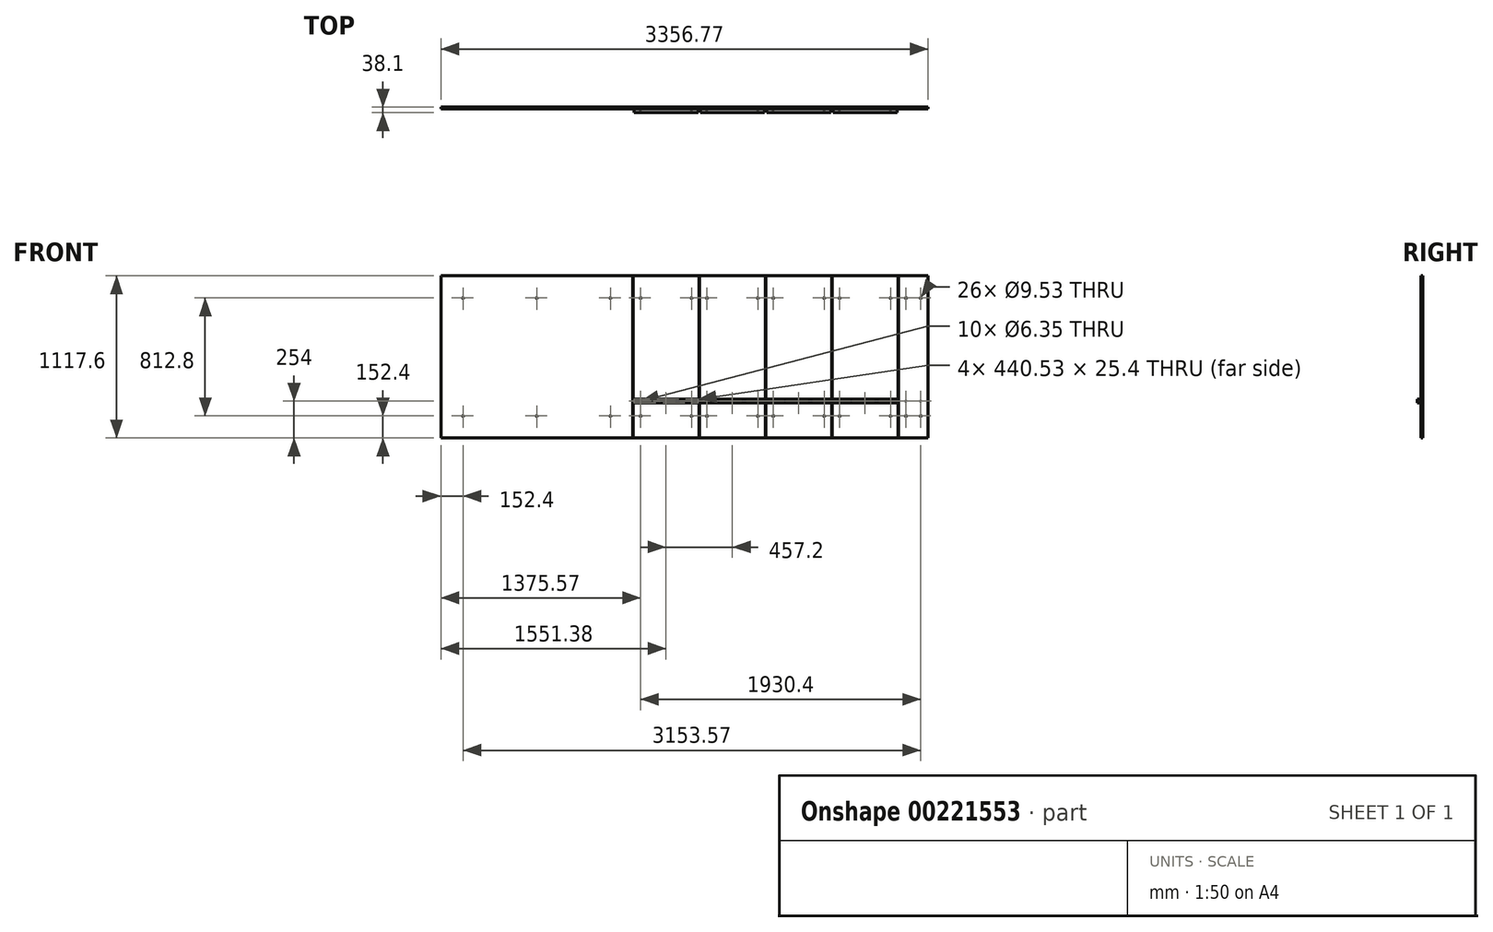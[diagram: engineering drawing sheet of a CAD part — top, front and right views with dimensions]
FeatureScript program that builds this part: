
annotation { "Feature Type Name" : "Feature", "Feature Type Description" : "" }
export const myFeature = defineFeature(function(context is Context, id is Id, definition is map)
    precondition{}
    {
        {
            var Q0;
            Q0=qCreatedBy(makeId("Front.planeOp"),FACE);
            var sketch = newSketch(context, id + "F0", { "sketchPlane" : qUnion([Q0])});
            skLineSegment(sketch, "E0.bottom", {"start": v(0, 0) * mm, "end": v(1320.8, 0) * mm});
            skLineSegment(sketch, "E0.top", {"start": v(0, 1117.6) * mm, "end": v(1320.8, 1117.6) * mm});
            skLineSegment(sketch, "E0.left", {"start": v(0, 0) * mm, "end": v(0, 1117.6) * mm});
            skLineSegment(sketch, "E0.right", {"start": v(1320.8, 0) * mm, "end": v(1320.8, 1117.6) * mm});
            skLineSegment(sketch, "E1.bottom", {"start": v(1320.8, 0) * mm, "end": v(1324.77, 0) * mm});
            skLineSegment(sketch, "E1.top", {"start": v(1320.8, 1117.6) * mm, "end": v(1324.77, 1117.6) * mm});
            skLineSegment(sketch, "E1.right", {"start": v(1324.77, 0) * mm, "end": v(1324.77, 1117.6) * mm});
            skLineSegment(sketch, "E2.bottom", {"start": v(1324.77, 0) * mm, "end": v(1778, 0) * mm});
            skLineSegment(sketch, "E2.top", {"start": v(1324.77, 1117.6) * mm, "end": v(1778, 1117.6) * mm});
            skLineSegment(sketch, "E2.right", {"start": v(1778, 0) * mm, "end": v(1778, 1117.6) * mm});
            skLineSegment(sketch, "E3.1.0.1", {"start": v(1781.97, 1117.6) * mm, "end": v(2235.2, 1117.6) * mm});
            skLineSegment(sketch, "E3.1.0.2", {"start": v(2235.2, 0) * mm, "end": v(2235.2, 1117.6) * mm});
            skLineSegment(sketch, "E3.1.0.3", {"start": v(1781.97, 0) * mm, "end": v(1781.97, 1117.6) * mm});
            skLineSegment(sketch, "E3.1.0.4", {"start": v(1781.97, 0) * mm, "end": v(1781.97, 1117.6) * mm});
            skLineSegment(sketch, "E3.1.0.6", {"start": v(1778, 1117.6) * mm, "end": v(1781.97, 1117.6) * mm});
            skLineSegment(sketch, "E3.1.0.7", {"start": v(1781.97, 0) * mm, "end": v(2235.2, 0) * mm});
            skLineSegment(sketch, "E3.1.0.8", {"start": v(1778, 0) * mm, "end": v(1781.97, 0) * mm});
            skLineSegment(sketch, "E3.2.0.0", {"start": v(2235.2, 0) * mm, "end": v(2235.2, 1117.6) * mm});
            skLineSegment(sketch, "E3.2.0.1", {"start": v(2239.17, 1117.6) * mm, "end": v(2692.4, 1117.6) * mm});
            skLineSegment(sketch, "E3.2.0.2", {"start": v(2692.4, 0) * mm, "end": v(2692.4, 1117.6) * mm});
            skLineSegment(sketch, "E3.2.0.3", {"start": v(2239.17, 0) * mm, "end": v(2239.17, 1117.6) * mm});
            skLineSegment(sketch, "E3.2.0.4", {"start": v(2239.17, 0) * mm, "end": v(2239.17, 1117.6) * mm});
            skLineSegment(sketch, "E3.2.0.5", {"start": v(2235.2, 0) * mm, "end": v(2235.2, 1117.6) * mm});
            skLineSegment(sketch, "E3.2.0.6", {"start": v(2235.2, 1117.6) * mm, "end": v(2239.17, 1117.6) * mm});
            skLineSegment(sketch, "E3.2.0.7", {"start": v(2239.17, 0) * mm, "end": v(2692.4, 0) * mm});
            skLineSegment(sketch, "E3.2.0.8", {"start": v(2235.2, 0) * mm, "end": v(2239.17, 0) * mm});
            skLineSegment(sketch, "E3.direction1", {"start": v(1320.8, 0) * mm, "end": v(1778, 0) * mm, "construction": true});
            skLineSegment(sketch, "E4.3.3.0", {"start": v(2696.37, 1117.6) * mm, "end": v(3149.6, 1117.6) * mm});
            skLineSegment(sketch, "E4.6.3.0", {"start": v(3149.6, 0) * mm, "end": v(3149.6, 1117.6) * mm});
            skLineSegment(sketch, "E4.9.3.0", {"start": v(2696.37, 0) * mm, "end": v(2696.37, 1117.6) * mm});
            skLineSegment(sketch, "E4.12.3.0", {"start": v(2696.37, 0) * mm, "end": v(2696.37, 1117.6) * mm});
            skLineSegment(sketch, "E4.18.3.0", {"start": v(2692.4, 1117.6) * mm, "end": v(2696.37, 1117.6) * mm});
            skLineSegment(sketch, "E4.21.3.0", {"start": v(2696.37, 0) * mm, "end": v(3149.6, 0) * mm});
            skLineSegment(sketch, "E4.24.3.0", {"start": v(2692.4, 0) * mm, "end": v(2696.37, 0) * mm});
            skLineSegment(sketch, "E5.9.4.0", {"start": v(3153.57, 0) * mm, "end": v(3153.57, 1117.6) * mm});
            skLineSegment(sketch, "E5.12.4.0", {"start": v(3153.57, 0) * mm, "end": v(3153.57, 1117.6) * mm});
            skLineSegment(sketch, "E5.18.4.0", {"start": v(3149.6, 1117.6) * mm, "end": v(3153.57, 1117.6) * mm});
            skLineSegment(sketch, "E5.24.4.0", {"start": v(3149.6, 0) * mm, "end": v(3153.57, 0) * mm});
            skLineSegment(sketch, "E6.bottom", {"start": v(3153.57, 0) * mm, "end": v(3356.77, 0) * mm});
            skLineSegment(sketch, "E6.top", {"start": v(3153.57, 1117.6) * mm, "end": v(3356.77, 1117.6) * mm});
            skLineSegment(sketch, "E6.right", {"start": v(3356.77, 0) * mm, "end": v(3356.77, 1117.6) * mm});
            skPoint(sketch, "E7.firstSnap0", {"position": v(0, 558.8) * mm});
            skLineSegment(sketch, "E7.bottom", {"start": v(-26.7, 558.8) * mm, "end": v(0, 558.8) * mm});
            skLineSegment(sketch, "E7.top", {"start": v(-26.7, 558.8) * mm, "end": v(0, 558.8) * mm});
            skLineSegment(sketch, "E7.left", {"start": v(-26.7, 558.8) * mm, "end": v(-26.7, 558.8) * mm});
            skLineSegment(sketch, "E7.right", {"start": v(0, 558.8) * mm, "end": v(0, 558.8) * mm});
            skLineSegment(sketch, "E8", {"start": v(0, 0) * mm, "end": v(0, 152.4) * mm});
            skLineSegment(sketch, "E9", {"start": v(0, 152.4) * mm, "end": v(152.4, 152.4) * mm});
            skLineSegment(sketch, "E10", {"start": v(152.4, 152.4) * mm, "end": v(660.4, 152.4) * mm});
            skLineSegment(sketch, "E11", {"start": v(660.4, 152.4) * mm, "end": v(1168.4, 152.4) * mm});
            skLineSegment(sketch, "E12", {"start": v(1168.4, 152.4) * mm, "end": v(1168.4, 965.2) * mm});
            skLineSegment(sketch, "E13", {"start": v(1168.4, 965.2) * mm, "end": v(660.4, 965.2) * mm});
            skLineSegment(sketch, "E14", {"start": v(660.4, 965.2) * mm, "end": v(152.4, 965.2) * mm});
            skCircle(sketch, "E15", {"center": v(152.4, 965.2) * mm, "radius": 4.76 * mm});
            skCircle(sketch, "E16", {"center": v(660.4, 965.2) * mm, "radius": 4.76 * mm});
            skCircle(sketch, "E17", {"center": v(1168.4, 965.2) * mm, "radius": 4.76 * mm});
            skCircle(sketch, "E18", {"center": v(152.4, 152.4) * mm, "radius": 4.76 * mm});
            skCircle(sketch, "E19", {"center": v(660.4, 152.4) * mm, "radius": 4.76 * mm});
            skCircle(sketch, "E20", {"center": v(1168.4, 152.4) * mm, "radius": 4.76 * mm});
            skLineSegment(sketch, "E21", {"start": v(1168.4, 152.4) * mm, "end": v(1320.8, 152.4) * mm});
            skLineSegment(sketch, "E22", {"start": v(1320.8, 152.4) * mm, "end": v(1324.77, 152.28) * mm});
            skLineSegment(sketch, "E23", {"start": v(1324.77, 152.28) * mm, "end": v(1375.57, 152.4) * mm});
            skPoint(sketch, "E24.endSnap0", {"position": v(1244.6, 152.4) * mm});
            skLineSegment(sketch, "E25", {"start": v(1778, 152.4) * mm, "end": v(1727.2, 152.4) * mm});
            skCircle(sketch, "E26", {"center": v(1375.57, 152.4) * mm, "radius": 4.76 * mm});
            skCircle(sketch, "E27", {"center": v(1727.2, 152.4) * mm, "radius": 4.76 * mm});
            skCircle(sketch, "E28.0.1.0", {"center": v(1375.57, 965.2) * mm, "radius": 4.76 * mm});
            skCircle(sketch, "E28.0.1.1", {"center": v(1727.2, 965.2) * mm, "radius": 4.76 * mm});
            skCircle(sketch, "E28.1.0.0", {"center": v(1832.77, 152.4) * mm, "radius": 4.76 * mm});
            skCircle(sketch, "E28.1.0.1", {"center": v(2184.4, 152.4) * mm, "radius": 4.76 * mm});
            skCircle(sketch, "E28.1.1.0", {"center": v(1832.77, 965.2) * mm, "radius": 4.76 * mm});
            skCircle(sketch, "E28.1.1.1", {"center": v(2184.4, 965.2) * mm, "radius": 4.76 * mm});
            skCircle(sketch, "E28.2.0.0", {"center": v(2289.97, 152.4) * mm, "radius": 4.76 * mm});
            skCircle(sketch, "E28.2.0.1", {"center": v(2641.6, 152.4) * mm, "radius": 4.76 * mm});
            skCircle(sketch, "E28.2.1.0", {"center": v(2289.97, 965.2) * mm, "radius": 4.76 * mm});
            skCircle(sketch, "E28.2.1.1", {"center": v(2641.6, 965.2) * mm, "radius": 4.76 * mm});
            skCircle(sketch, "E28.3.0.0", {"center": v(2747.17, 152.4) * mm, "radius": 4.76 * mm});
            skCircle(sketch, "E28.3.0.1", {"center": v(3098.8, 152.4) * mm, "radius": 4.76 * mm});
            skCircle(sketch, "E28.3.1.0", {"center": v(2747.17, 965.2) * mm, "radius": 4.76 * mm});
            skCircle(sketch, "E28.3.1.1", {"center": v(3098.8, 965.2) * mm, "radius": 4.76 * mm});
            skCircle(sketch, "E28.4.0.0", {"center": v(3204.37, 152.4) * mm, "radius": 4.76 * mm});
            skCircle(sketch, "E28.4.1.0", {"center": v(3204.37, 965.2) * mm, "radius": 4.76 * mm});
            skLineSegment(sketch, "E28.direction1", {"start": v(1375.57, 152.4) * mm, "end": v(1832.77, 152.4) * mm, "construction": true});
            skLineSegment(sketch, "E28.direction2", {"start": v(1375.57, 152.4) * mm, "end": v(1375.57, 965.2) * mm, "construction": true});
            skLineSegment(sketch, "E29", {"start": v(3356.77, 152.4) * mm, "end": v(3305.97, 152.4) * mm});
            skLineSegment(sketch, "E30", {"start": v(3356.77, 965.2) * mm, "end": v(3305.97, 965.2) * mm});
            skCircle(sketch, "E31", {"center": v(3305.97, 965.2) * mm, "radius": 4.76 * mm});
            skCircle(sketch, "E32", {"center": v(3305.97, 152.4) * mm, "radius": 4.76 * mm});
            skLineSegment(sketch, "E33", {"start": v(1375.57, 152.4) * mm, "end": v(1375.57, 254) * mm});
            skLineSegment(sketch, "E34", {"start": v(1375.57, 254) * mm, "end": v(1375.57, 742.95) * mm});
            skCircle(sketch, "E35", {"center": v(1375.57, 254) * mm, "radius": 3.18 * mm});
            skLineSegment(sketch, "E36", {"start": v(1375.57, 254) * mm, "end": v(1727.2, 254) * mm});
            skCircle(sketch, "E37", {"center": v(1727.2, 254) * mm, "radius": 3.18 * mm});
            skCircle(sketch, "E38.1.0.0", {"center": v(1832.77, 254) * mm, "radius": 3.18 * mm});
            skCircle(sketch, "E38.1.0.1", {"center": v(2184.4, 254) * mm, "radius": 3.18 * mm});
            skCircle(sketch, "E38.2.0.0", {"center": v(2289.97, 254) * mm, "radius": 3.18 * mm});
            skCircle(sketch, "E38.2.0.1", {"center": v(2641.6, 254) * mm, "radius": 3.18 * mm});
            skCircle(sketch, "E38.3.0.0", {"center": v(2747.17, 254) * mm, "radius": 3.18 * mm});
            skCircle(sketch, "E38.3.0.1", {"center": v(3098.8, 254) * mm, "radius": 3.18 * mm});
            skCircle(sketch, "E38.4.0.0", {"center": v(3204.37, 254) * mm, "radius": 3.18 * mm});
            skCircle(sketch, "E38.4.0.1", {"center": v(3556, 254) * mm, "radius": 3.18 * mm});
            skLineSegment(sketch, "E38.direction1", {"start": v(1375.57, 254) * mm, "end": v(1832.77, 254) * mm, "construction": true});
            skLineSegment(sketch, "E39", {"start": v(1324.77, 254) * mm, "end": v(1331.12, 254) * mm});
            skLineSegment(sketch, "E40", {"start": v(1331.12, 254) * mm, "end": v(1331.12, 266.7) * mm});
            skLineSegment(sketch, "E41", {"start": v(1331.12, 266.7) * mm, "end": v(1331.12, 241.3) * mm});
            skLineSegment(sketch, "E42", {"start": v(1727.2, 254) * mm, "end": v(1778, 254) * mm});
            skLineSegment(sketch, "E43", {"start": v(1778, 254) * mm, "end": v(1771.65, 254) * mm});
            skLineSegment(sketch, "E44", {"start": v(1771.65, 254) * mm, "end": v(1771.65, 241.3) * mm});
            skLineSegment(sketch, "E45", {"start": v(1771.65, 241.3) * mm, "end": v(1331.12, 241.3) * mm});
            skLineSegment(sketch, "E46", {"start": v(1331.12, 266.7) * mm, "end": v(1771.65, 266.7) * mm});
            skLineSegment(sketch, "E47", {"start": v(1771.65, 266.7) * mm, "end": v(1771.65, 254) * mm});
            skLineSegment(sketch, "E48.1.0.0", {"start": v(2228.85, 241.3) * mm, "end": v(1788.32, 241.3) * mm});
            skLineSegment(sketch, "E48.1.0.1", {"start": v(2228.85, 254) * mm, "end": v(2228.85, 241.3) * mm});
            skLineSegment(sketch, "E48.1.0.2", {"start": v(1788.32, 266.7) * mm, "end": v(2228.85, 266.7) * mm});
            skLineSegment(sketch, "E48.1.0.3", {"start": v(2228.85, 266.7) * mm, "end": v(2228.85, 254) * mm});
            skLineSegment(sketch, "E48.1.0.4", {"start": v(1788.32, 266.7) * mm, "end": v(1788.32, 241.3) * mm});
            skLineSegment(sketch, "E48.2.0.0", {"start": v(2686.05, 241.3) * mm, "end": v(2245.52, 241.3) * mm});
            skLineSegment(sketch, "E48.2.0.1", {"start": v(2686.05, 254) * mm, "end": v(2686.05, 241.3) * mm});
            skLineSegment(sketch, "E48.2.0.2", {"start": v(2245.52, 266.7) * mm, "end": v(2686.05, 266.7) * mm});
            skLineSegment(sketch, "E48.2.0.3", {"start": v(2686.05, 266.7) * mm, "end": v(2686.05, 254) * mm});
            skLineSegment(sketch, "E48.2.0.4", {"start": v(2245.52, 266.7) * mm, "end": v(2245.52, 241.3) * mm});
            skLineSegment(sketch, "E48.3.0.0", {"start": v(3143.25, 241.3) * mm, "end": v(2702.72, 241.3) * mm});
            skLineSegment(sketch, "E48.3.0.1", {"start": v(3143.25, 254) * mm, "end": v(3143.25, 241.3) * mm});
            skLineSegment(sketch, "E48.3.0.2", {"start": v(2702.72, 266.7) * mm, "end": v(3143.25, 266.7) * mm});
            skLineSegment(sketch, "E48.3.0.3", {"start": v(3143.25, 266.7) * mm, "end": v(3143.25, 254) * mm});
            skLineSegment(sketch, "E48.3.0.4", {"start": v(2702.72, 266.7) * mm, "end": v(2702.72, 241.3) * mm});
            skLineSegment(sketch, "E48.direction1", {"start": v(1331.12, 241.3) * mm, "end": v(1788.32, 241.3) * mm, "construction": true});
            skSolve(sketch);
        }
        {
            var Q0;
            {var subQ17=sQuery(id+"F0.wireOp",EDGE,"E0.top");Q0=makeQuery(id+"F0.imprint","IMPRINT",FACE,{"disambiguationData":[TD([[makeQuery(id+"F0.imprint","IMPRINT",EDGE,{"derivedFrom":subQ17}),-1.0]])]});}
            var Q1;
            {var subQ5=sQuery(id+"F0.wireOp",EDGE,"E0.bottom");Q1=makeQuery(id+"F0.imprint","IMPRINT",FACE,{"disambiguationData":[TD([[makeQuery(id+"F0.imprint","IMPRINT",EDGE,{"derivedFrom":subQ5}),1.0]])]});}
            var Q2;
            {var subQ3=sQuery(id+"F0.wireOp",EDGE,"E2.bottom");Q2=makeQuery(id+"F0.imprint","IMPRINT",FACE,{"disambiguationData":[TD([[makeQuery(id+"F0.imprint","IMPRINT",EDGE,{"derivedFrom":subQ3}),1.0]])]});}
            var Q3;
            Q3=makeQuery(id+"F0.imprint","IMPRINT",FACE,{"disambiguationData":[TD([[makeQuery(id+"F0.imprint","IMPRINT",EDGE,{"derivedFrom":sQuery(id+"F0.wireOp",EDGE,"E3.1.0.1")}),-1.0]])]});
            var Q4;
            Q4=makeQuery(id+"F0.imprint","IMPRINT",FACE,{"disambiguationData":[TD([[makeQuery(id+"F0.imprint","IMPRINT",EDGE,{"derivedFrom":sQuery(id+"F0.wireOp",EDGE,"E3.2.0.1")}),-1.0]])]});
            var Q5;
            Q5=makeQuery(id+"F0.imprint","IMPRINT",FACE,{"disambiguationData":[TD([[makeQuery(id+"F0.imprint","IMPRINT",EDGE,{"derivedFrom":sQuery(id+"F0.wireOp",EDGE,"E4.3.3.0")}),-1.0]])]});
            var Q6;
            {var subQ1=sQuery(id+"F0.wireOp",EDGE,"E6.bottom");Q6=makeQuery(id+"F0.imprint","IMPRINT",FACE,{"disambiguationData":[TD([[makeQuery(id+"F0.imprint","IMPRINT",EDGE,{"derivedFrom":subQ1}),1.0]])]});}
            extrude(context, id + "F1", {"entities" : qUnion([Q0, Q1, Q2, Q3, Q4, Q5, Q6]), "depth" : 12.7 * mm});
        }
        {
            var Q0;
            Q0=makeQuery(id+"F1.opExtrude","CAP_FACE",FACE,{"disambiguationData":[OSD([sQuery(id+"F0.wireOp",EDGE,"E6.bottom"),sQuery(id+"F0.wireOp",EDGE,"E6.top"),sQuery(id+"F0.wireOp",EDGE,"E5.9.4.0"),sQuery(id+"F0.wireOp",EDGE,"E6.right"),sQuery(id+"F0.wireOp",EDGE,"E28.4.0.0"),sQuery(id+"F0.wireOp",EDGE,"E28.4.1.0"),sQuery(id+"F0.wireOp",EDGE,"E31"),sQuery(id+"F0.wireOp",EDGE,"E32"),sQuery(id+"F0.wireOp",EDGE,"E38.4.0.0")])],"isStart":false});
            var sketch = newSketch(context, id + "F2", { "sketchPlane" : qUnion([Q0])});
            skLineSegment(sketch, "E49", {"start": v(3204.37, 254) * mm, "end": v(3305.97, 254) * mm});
            skCircle(sketch, "E50", {"center": v(3305.97, 254) * mm, "radius": 3.18 * mm});
            skSolve(sketch);
        }
        {
            var Q0;
            Q0=makeQuery(id+"F2.imprint","IMPRINT",FACE,{"disambiguationData":[TD([[makeQuery(id+"F2.imprint","IMPRINT",EDGE,{"derivedFrom":sQuery(id+"F2.wireOp",EDGE,"E50")}),1.0]])]});
            extrude(context, id + "F3", {"entities" : qUnion([Q0]), "operationType" : NewBodyOperationType.REMOVE, "oppositeDirection" : true, "depth" : 12.7 * mm});
        }
        {
            var Q0;
            {var subQ6=sQuery(id+"F0.wireOp",EDGE,"E2.top");Q0=makeQuery(id+"F0.imprint","IMPRINT",FACE,{"disambiguationData":[TD([[makeQuery(id+"F0.imprint","IMPRINT",EDGE,{"derivedFrom":subQ6}),-1.0]])]});}
            var Q1;
            {var subQ10=sQuery(id+"F0.wireOp",EDGE,"E39");Q1=makeQuery(id+"F0.imprint","IMPRINT",FACE,{"disambiguationData":[TD([[makeQuery(id+"F0.imprint","IMPRINT",EDGE,{"derivedFrom":subQ10}),-1.0]])]});}
            extrude(context, id + "F4", {"entities" : qUnion([Q0, Q1]), "operationType" : NewBodyOperationType.ADD, "depth" : 12.7 * mm});
        }
        {
            var Q0;
            {var subQ11=sQuery(id+"F0.wireOp",EDGE,"E47");Q0=makeQuery(id+"F0.imprint","IMPRINT",FACE,{"disambiguationData":[TD([[makeQuery(id+"F0.imprint","IMPRINT",EDGE,{"derivedFrom":subQ11}),-1.0]])]});}
            var Q1;
            {var subQ5=sQuery(id+"F0.wireOp",EDGE,"E33");var subQ10=sQuery(id+"F0.wireOp",EDGE,"E45");var subQ11=makeQuery(id+"F0.imprint","INTERSECT",VERTEX,{"derivedFrom":[subQ5,subQ10]});Q1=makeQuery(id+"F0.imprint","IMPRINT",FACE,{"disambiguationData":[TD([[makeQuery(id+"F0.imprint","IMPRINT",EDGE,{"disambiguationData":[TD([[subQ11,-1.0]])],"derivedFrom":subQ5}),1.0]])]});}
            var Q2;
            Q2=makeQuery(id+"F0.imprint","IMPRINT",FACE,{"disambiguationData":[TD([[makeQuery(id+"F0.imprint","IMPRINT",EDGE,{"derivedFrom":sQuery(id+"F0.wireOp",EDGE,"E38.1.0.0")}),-1.0]])]});
            var Q3;
            {var subQ11=sQuery(id+"F0.wireOp",EDGE,"E44");Q3=makeQuery(id+"F0.imprint","IMPRINT",FACE,{"disambiguationData":[TD([[makeQuery(id+"F0.imprint","IMPRINT",EDGE,{"derivedFrom":subQ11}),-1.0]])]});}
            var Q4;
            Q4=makeQuery(id+"F0.imprint","IMPRINT",FACE,{"disambiguationData":[TD([[makeQuery(id+"F0.imprint","IMPRINT",EDGE,{"derivedFrom":sQuery(id+"F0.wireOp",EDGE,"E38.2.0.0")}),-1.0]])]});
            var Q5;
            Q5=makeQuery(id+"F0.imprint","IMPRINT",FACE,{"disambiguationData":[TD([[makeQuery(id+"F0.imprint","IMPRINT",EDGE,{"derivedFrom":sQuery(id+"F0.wireOp",EDGE,"E38.3.0.0")}),-1.0]])]});
            extrude(context, id + "F5", {"entities" : qUnion([Q0, Q1, Q2, Q3, Q4, Q5]), "depth" : 38.1 * mm});
        }
    });
